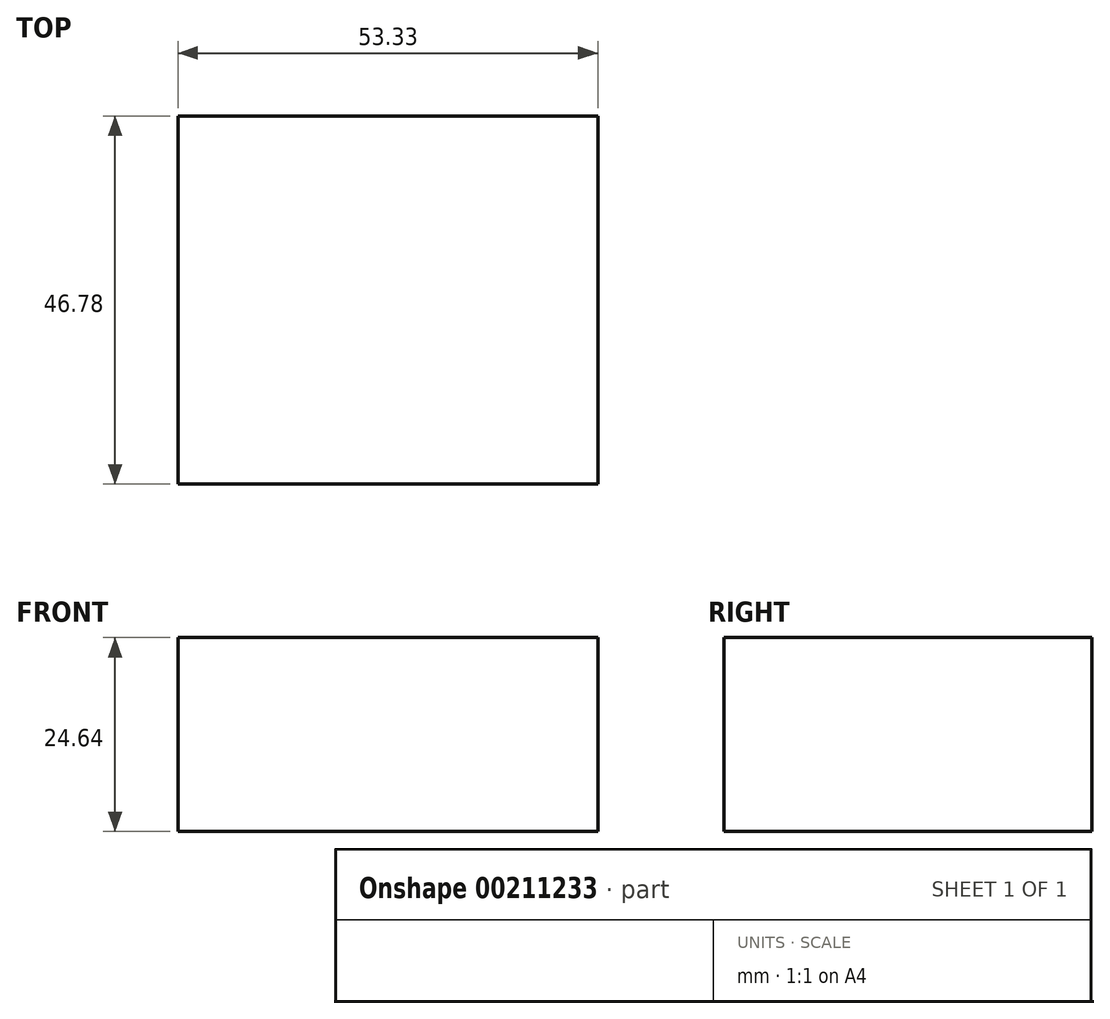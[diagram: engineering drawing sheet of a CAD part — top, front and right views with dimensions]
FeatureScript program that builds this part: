
annotation { "Feature Type Name" : "Feature", "Feature Type Description" : "" }
export const myFeature = defineFeature(function(context is Context, id is Id, definition is map)
    precondition{}
    {
        {
            var Q0;
            Q0=qCreatedBy(makeId("Top.planeOp"),FACE);
            var sketch = newSketch(context, id + "F0", { "sketchPlane" : qUnion([Q0])});
            skLineSegment(sketch, "E0.bottom", {"start": v(0, 0) * mm, "end": v(0, 0) * mm});
            skLineSegment(sketch, "E0.top", {"start": v(0, 46.78) * mm, "end": v(0, 46.78) * mm});
            skLineSegment(sketch, "E0.left", {"start": v(0, 0) * mm, "end": v(0, 46.78) * mm});
            skLineSegment(sketch, "E0.right", {"start": v(0, 0) * mm, "end": v(0, 46.78) * mm});
            skLineSegment(sketch, "E1.bottom", {"start": v(0, 46.78) * mm, "end": v(53.33, 46.78) * mm});
            skLineSegment(sketch, "E1.top", {"start": v(0, 0) * mm, "end": v(53.33, 0) * mm});
            skLineSegment(sketch, "E1.left", {"start": v(0, 46.78) * mm, "end": v(0, 0) * mm});
            skLineSegment(sketch, "E1.right", {"start": v(53.33, 46.78) * mm, "end": v(53.33, 0) * mm});
            skSolve(sketch);
        }
        {
            var Q0;
            Q0=makeQuery(id+"F0.imprint","IMPRINT",FACE,{"disambiguationData":[TD([[makeQuery(id+"F0.imprint","IMPRINT",EDGE,{"derivedFrom":sQuery(id+"F0.wireOp",EDGE,"E1.bottom")}),-1.0]])]});
            extrude(context, id + "F1", {"entities" : qUnion([Q0]), "depth" : 24.64 * mm});
        }
    });
